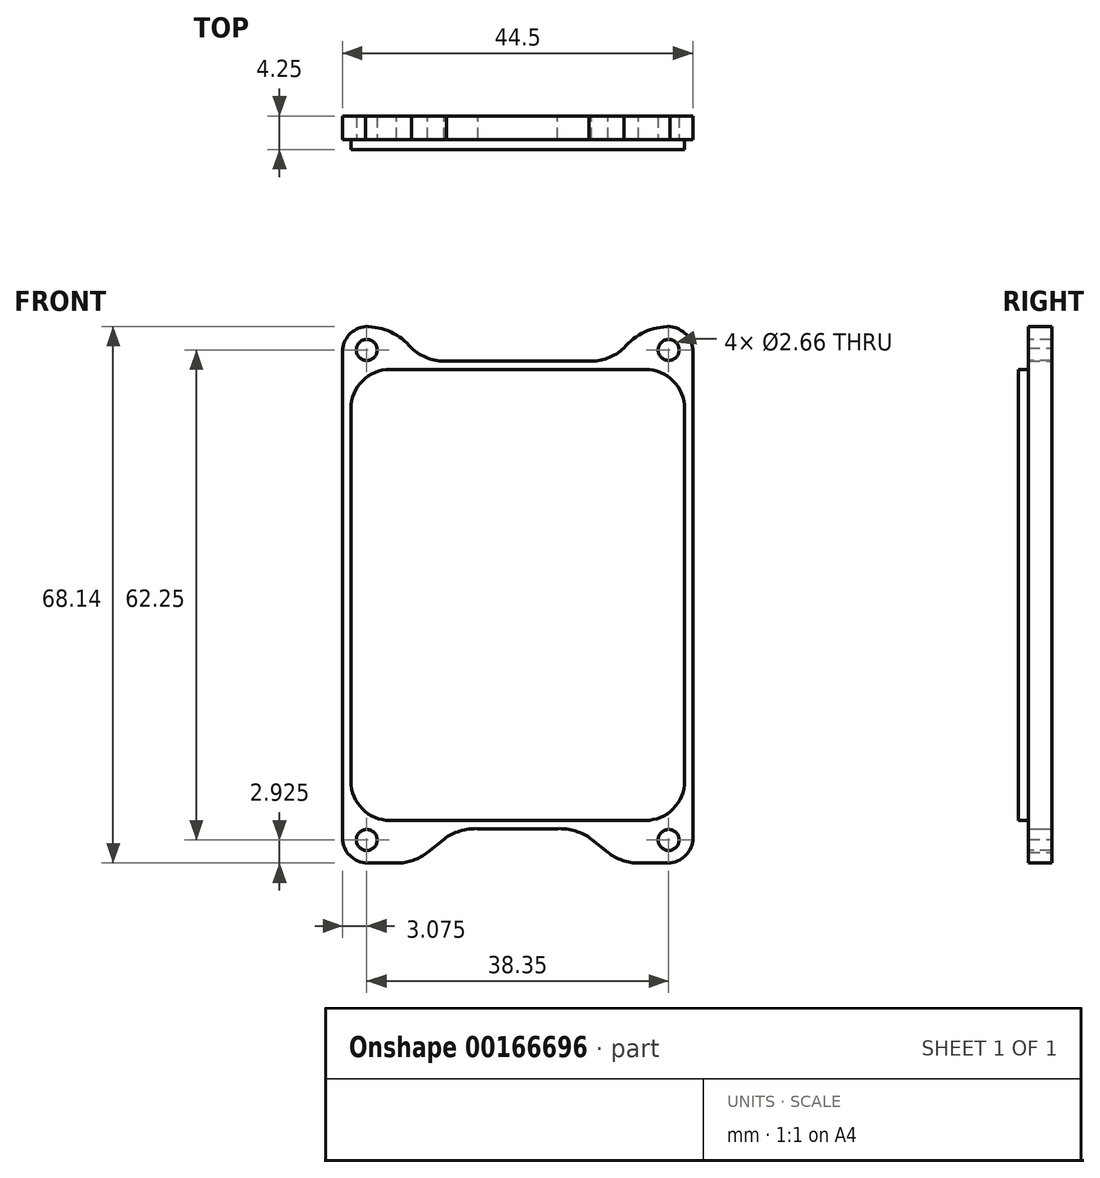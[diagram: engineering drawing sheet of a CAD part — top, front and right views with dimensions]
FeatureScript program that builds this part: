
annotation { "Feature Type Name" : "Feature", "Feature Type Description" : "" }
export const myFeature = defineFeature(function(context is Context, id is Id, definition is map)
    precondition{}
    {
        {
            var Q0;
            Q0=qCreatedBy(makeId("Front.planeOp"),FACE);
            var sketch = newSketch(context, id + "F0", { "sketchPlane" : qUnion([Q0])});
            skLineSegment(sketch, "E0", {"start": v(-22.25, 30.9) * mm, "end": v(-22.25, -30.86) * mm});
            skArc(sketch, "E1", {"start": v(-19.36, 34.09) * mm, "mid": v(-21.42, 33.05) * mm, "end": v(-22.25, 30.9) * mm});
            skArc(sketch, "E2", {"start": v(-13.5, 31.38) * mm, "mid": v(-16.12, 33.4) * mm, "end": v(-19.36, 34.09) * mm});
            skArc(sketch, "E3", {"start": v(-13.5, 31.38) * mm, "mid": v(-11.43, 30.08) * mm, "end": v(-9.03, 29.7) * mm});
            skLineSegment(sketch, "E4", {"start": v(-9.03, 29.7) * mm, "end": v(0, 29.7) * mm});
            skArc(sketch, "E5", {"start": v(-22.25, -30.86) * mm, "mid": v(-21.33, -33.1) * mm, "end": v(-19.1, -34.04) * mm});
            skArc(sketch, "E6", {"start": v(-15.37, -34.04) * mm, "mid": v(-13.28, -33.72) * mm, "end": v(-11.44, -32.68) * mm});
            skArc(sketch, "E7", {"start": v(-5.04, -29.7) * mm, "mid": v(-7.33, -29.98) * mm, "end": v(-9.39, -31.04) * mm});
            skLineSegment(sketch, "E8", {"start": v(-19.1, -34.04) * mm, "end": v(-15.37, -34.04) * mm});
            skLineSegment(sketch, "E9", {"start": v(-11.44, -32.68) * mm, "end": v(-9.39, -31.04) * mm});
            skLineSegment(sketch, "E10", {"start": v(-5.04, -29.7) * mm, "end": v(0, -29.7) * mm});
            skArc(sketch, "E11.MirrorCS", {"start": v(5.04, -29.7) * mm, "mid": v(7.33, -29.98) * mm, "end": v(9.39, -31.04) * mm});
            skArc(sketch, "E12.MirrorCS", {"start": v(19.36, 34.09) * mm, "mid": v(21.42, 33.05) * mm, "end": v(22.25, 30.9) * mm});
            skArc(sketch, "E13.MirrorCS", {"start": v(13.5, 31.38) * mm, "mid": v(16.12, 33.4) * mm, "end": v(19.36, 34.09) * mm});
            skArc(sketch, "E14.MirrorCS", {"start": v(13.5, 31.38) * mm, "mid": v(11.43, 30.08) * mm, "end": v(9.03, 29.7) * mm});
            skLineSegment(sketch, "E15.MirrorCS", {"start": v(11.44, -32.68) * mm, "end": v(9.39, -31.04) * mm});
            skArc(sketch, "E16.MirrorCS", {"start": v(22.25, -30.86) * mm, "mid": v(21.33, -33.1) * mm, "end": v(19.1, -34.04) * mm});
            skArc(sketch, "E17.MirrorCS", {"start": v(15.37, -34.04) * mm, "mid": v(13.28, -33.72) * mm, "end": v(11.44, -32.68) * mm});
            skLineSegment(sketch, "E18.MirrorCS", {"start": v(19.1, -34.04) * mm, "end": v(15.37, -34.04) * mm});
            skLineSegment(sketch, "E19.MirrorCS", {"start": v(5.04, -29.7) * mm, "end": v(0, -29.7) * mm});
            skLineSegment(sketch, "E20.MirrorCS", {"start": v(22.25, 30.9) * mm, "end": v(22.25, -30.86) * mm});
            skLineSegment(sketch, "E21.MirrorCS", {"start": v(9.03, 29.7) * mm, "end": v(0, 29.7) * mm});
            skLineSegment(sketch, "E22", {"start": v(-19.04, 30.9) * mm, "end": v(19.04, 30.9) * mm, "construction": true});
            skLineSegment(sketch, "E23", {"start": v(-19.26, 26.6) * mm, "end": v(19.26, 26.6) * mm, "construction": true});
            skLineSegment(sketch, "E24", {"start": v(-9.29, 35.78) * mm, "end": v(9.29, 35.78) * mm, "construction": true});
            skLineSegment(sketch, "E25", {"start": v(-15.2, -28.18) * mm, "end": v(15.2, -28.18) * mm, "construction": true});
            skLineSegment(sketch, "E26", {"start": v(-19.07, -30.86) * mm, "end": v(19.07, -30.86) * mm, "construction": true});
            skLineSegment(sketch, "E27", {"start": v(-5.4, -36.28) * mm, "end": v(5.4, -36.28) * mm, "construction": true});
            skSolve(sketch);
        }
        {
            var Q0;
            Q0 = qSketchRegion(id + "F0", true);
            extrude(context, id + "F1", {"entities" : qUnion([Q0]), "depth" : 3 * mm});
        }
        {
            var Q0;
            Q0=makeQuery(id+"F1.opExtrude","CAP_FACE",FACE,{"disambiguationData":[OSD([sQuery(id+"F0.wireOp",EDGE,"E0"),sQuery(id+"F0.wireOp",EDGE,"E1"),sQuery(id+"F0.wireOp",EDGE,"E2"),sQuery(id+"F0.wireOp",EDGE,"E3"),sQuery(id+"F0.wireOp",EDGE,"E4"),sQuery(id+"F0.wireOp",EDGE,"E5"),sQuery(id+"F0.wireOp",EDGE,"E6"),sQuery(id+"F0.wireOp",EDGE,"E7"),sQuery(id+"F0.wireOp",EDGE,"E8"),sQuery(id+"F0.wireOp",EDGE,"E9"),sQuery(id+"F0.wireOp",EDGE,"E10"),sQuery(id+"F0.wireOp",EDGE,"E11.MirrorCS"),sQuery(id+"F0.wireOp",EDGE,"E12.MirrorCS"),sQuery(id+"F0.wireOp",EDGE,"E13.MirrorCS"),sQuery(id+"F0.wireOp",EDGE,"E14.MirrorCS"),sQuery(id+"F0.wireOp",EDGE,"E15.MirrorCS"),sQuery(id+"F0.wireOp",EDGE,"E16.MirrorCS"),sQuery(id+"F0.wireOp",EDGE,"E17.MirrorCS"),sQuery(id+"F0.wireOp",EDGE,"E18.MirrorCS"),sQuery(id+"F0.wireOp",EDGE,"E19.MirrorCS"),sQuery(id+"F0.wireOp",EDGE,"E20.MirrorCS"),sQuery(id+"F0.wireOp",EDGE,"E21.MirrorCS")])],"isStart":false});
            var sketch = newSketch(context, id + "F2", { "sketchPlane" : qUnion([Q0])});
            skLineSegment(sketch, "E28.bottom", {"start": v(-16.2, 28.65) * mm, "end": v(16.2, 28.65) * mm});
            skLineSegment(sketch, "E28.top", {"start": v(-16.2, -28.65) * mm, "end": v(16.2, -28.65) * mm});
            skLineSegment(sketch, "E28.left", {"start": v(-21.2, 23.65) * mm, "end": v(-21.2, -23.65) * mm});
            skLineSegment(sketch, "E28.right", {"start": v(21.2, 23.65) * mm, "end": v(21.2, -23.65) * mm});
            skPoint(sketch, "E29.visualSharp", {"position": v(-21.2, 28.65) * mm});
            skArc(sketch, "E29.filletArc", {"start": v(-16.2, 28.65) * mm, "mid": v(-19.74, 27.19) * mm, "end": v(-21.2, 23.65) * mm});
            skPoint(sketch, "E30.visualSharp", {"position": v(21.2, 28.65) * mm});
            skArc(sketch, "E30.filletArc", {"start": v(21.2, 23.65) * mm, "mid": v(19.74, 27.19) * mm, "end": v(16.2, 28.65) * mm});
            skPoint(sketch, "E31.visualSharp", {"position": v(21.2, -28.65) * mm});
            skArc(sketch, "E31.filletArc", {"start": v(16.2, -28.65) * mm, "mid": v(19.74, -27.19) * mm, "end": v(21.2, -23.65) * mm});
            skPoint(sketch, "E32.visualSharp", {"position": v(-21.2, -28.65) * mm});
            skArc(sketch, "E32.filletArc", {"start": v(-21.2, -23.65) * mm, "mid": v(-19.74, -27.19) * mm, "end": v(-16.2, -28.65) * mm});
            skSolve(sketch);
        }
        {
            var Q0;
            Q0 = qSketchRegion(id + "F2", true);
            extrude(context, id + "F3", {"entities" : qUnion([Q0]), "operationType" : NewBodyOperationType.ADD, "depth" : 1.25 * mm});
        }
        {
            var Q0;
            Q0=makeQuery(id+"F1.opExtrude","CAP_FACE",FACE,{"disambiguationData":[OSD([sQuery(id+"F0.wireOp",EDGE,"E0"),sQuery(id+"F0.wireOp",EDGE,"E1"),sQuery(id+"F0.wireOp",EDGE,"E2"),sQuery(id+"F0.wireOp",EDGE,"E3"),sQuery(id+"F0.wireOp",EDGE,"E4"),sQuery(id+"F0.wireOp",EDGE,"E5"),sQuery(id+"F0.wireOp",EDGE,"E6"),sQuery(id+"F0.wireOp",EDGE,"E7"),sQuery(id+"F0.wireOp",EDGE,"E8"),sQuery(id+"F0.wireOp",EDGE,"E9"),sQuery(id+"F0.wireOp",EDGE,"E10"),sQuery(id+"F0.wireOp",EDGE,"E11.MirrorCS"),sQuery(id+"F0.wireOp",EDGE,"E12.MirrorCS"),sQuery(id+"F0.wireOp",EDGE,"E13.MirrorCS"),sQuery(id+"F0.wireOp",EDGE,"E14.MirrorCS"),sQuery(id+"F0.wireOp",EDGE,"E15.MirrorCS"),sQuery(id+"F0.wireOp",EDGE,"E16.MirrorCS"),sQuery(id+"F0.wireOp",EDGE,"E17.MirrorCS"),sQuery(id+"F0.wireOp",EDGE,"E18.MirrorCS"),sQuery(id+"F0.wireOp",EDGE,"E19.MirrorCS"),sQuery(id+"F0.wireOp",EDGE,"E20.MirrorCS"),sQuery(id+"F0.wireOp",EDGE,"E21.MirrorCS")])],"isStart":false});
            var sketch = newSketch(context, id + "F4", { "sketchPlane" : qUnion([Q0])});
            skCircle(sketch, "E33", {"center": v(-19.17, 31.12) * mm, "radius": 1.33 * mm});
            skCircle(sketch, "E34", {"center": v(19.17, 31.12) * mm, "radius": 1.33 * mm});
            skCircle(sketch, "E35", {"center": v(19.17, -31.12) * mm, "radius": 1.33 * mm});
            skCircle(sketch, "E36", {"center": v(-19.17, -31.12) * mm, "radius": 1.33 * mm});
            skLineSegment(sketch, "E37", {"start": v(-19.17, 31.12) * mm, "end": v(19.17, 31.12) * mm, "construction": true});
            skLineSegment(sketch, "E38", {"start": v(-19.17, -31.12) * mm, "end": v(19.17, -31.12) * mm, "construction": true});
            skLineSegment(sketch, "E39", {"start": v(19.17, -31.12) * mm, "end": v(19.17, 31.12) * mm, "construction": true});
            skLineSegment(sketch, "E40", {"start": v(-19.17, 31.12) * mm, "end": v(-19.17, -31.12) * mm, "construction": true});
            skSolve(sketch);
        }
        {
            var Q0;
            Q0 = qSketchRegion(id + "F4", true);
            extrude(context, id + "F5", {"entities" : qUnion([Q0]), "operationType" : NewBodyOperationType.REMOVE, "endBound" : BoundingType.THROUGH_ALL, "oppositeDirection" : true, "depth" : 25 * mm});
        }
    });
